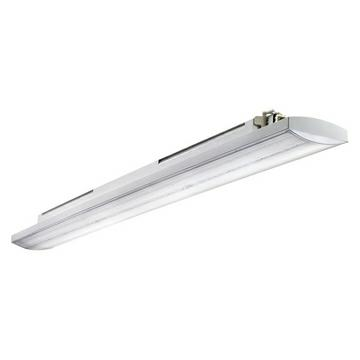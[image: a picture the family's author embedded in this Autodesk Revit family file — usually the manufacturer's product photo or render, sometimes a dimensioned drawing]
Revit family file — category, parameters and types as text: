
# Revit family: Lighting-Industriale-GEWISS-SMART[3]PLUS-PLAFONIERA-LED-EMERGENZA_TRANSPARENTE_1600mm
name_source: partatom
category: Apparecchi per illuminazione
units: mm (PartAtom-declared; Revit-internal decimal feet)

## family parameters
Condiviso = No
Host = Superficie
Punto di calcolo locali = No
Quota connettore circolare = Usa diametro
Sorgente d'illuminazione = No
Taglio con vuoti quando caricato = No
Tipo di parte = Normale

## types (1)
- Lighting-Industriale-GEWISS-SMART[3]PLUS-PLAFONIERA-LED-EMERGENZA_TRANSPARENTE_1600mm
    Applicazione = Interno
    Carico apparente = 53 VA
    Catalogo = LIGHTING
    Catalogo Serie = SMART[3] PLUS
    Classe di efficienza LED integrati = A ÷ A++
    Classe isolamento = II
    Codice Electrocod = 2434
    Commenti sul wattaggio = 53W
    Descrizione = SMART3 PLUS 1600 EMERG DT1+DT6 HE TRASP 9 57
    Ganci = Alluminio
    Garanzia = ND
    Glow Wire Test = 850°C
    Grado di protezione = IP66/IP69
    IDF = 3367e788-7319-4524-bfc4-ced9b5314006
    IDT = e64a989e-ee90-4262-bf48-8a52b238cc43
    Immagine tipo = GWS3258T30K.jpg
    Lampada = LED
    Lampada: = LED
    Lumen output (lm) = 5900
    Lunghezza = 1600 mm
    Lunghezza Lampada = 1600 mm
    Modello = GWS3325AT957
    Numero poli = 2
    Potenza di sistema = 50 W
    Produttore = GEWISS S.p.A.
    Prospetto di default = 1219 mm
    Resistenza agli urti = IK08
    SEO = Plafoniera
    Scheda Tecnica = https://www.gewiss.com
    Schermo = Trasparente
    Schermo. = Led Acceso
    Stampa 1_100 = Sì
    Stampa 1_200 = No
    Struttura = GRIGIO
    Temperatura di colore = 5700 K (CRI > 90)
    Temperatura di colore: = 5700 K (CRI > 90)
    Temperatura di funzionamento = ND
    Temperatura di utilizzo = ND
    Tensione = 220-240 V
    Tipologia sorgente luminosa = LED - Non sostituibile
    URL = https://www.gewiss.com
    Versione file RFA = 20.0
